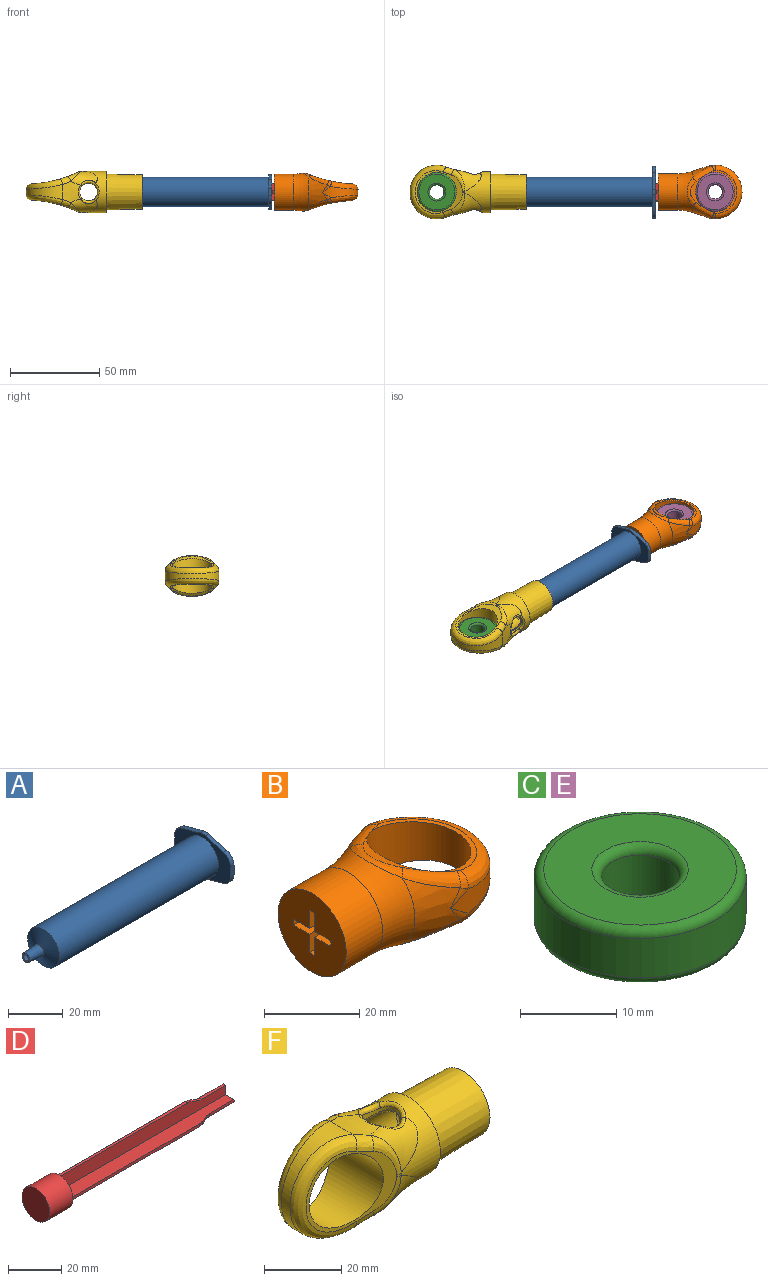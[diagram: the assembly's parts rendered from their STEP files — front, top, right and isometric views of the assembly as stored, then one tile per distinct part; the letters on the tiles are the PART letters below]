
ASSEMBLY  parts=6 mates=10
PART A: 21 faces, bbox 93.5x29x19.6 mm
  f0: cone r=2mm half-angle=3.3deg, axis (1,0,0), area 96.2mm2, adj f1,f6
  f1: plane 4x4mm, normal (-1,0,0), area 7.3mm2, adj f0,f2
  f2: cone r=1.3mm half-angle=3.3deg, axis (1,0,0), area 73.8mm2, adj f1,f3
  f3: cone r=7.31mm half-angle=69deg, axis (1,0,0), area 169.6mm2, adj f2,f4
  f4: cylinder r=7.31mm len=83.65mm, axis (-1,0,0), area 3842.3mm2, adj f3,f13
  f5: cylinder r=8.25mm len=82.5mm, axis (-1,0,0), area 4276.5mm2, adj f6,f14
  f6: cone r=2.4mm half-angle=69deg, axis (1,0,0), area 209.7mm2, adj f0,f5
  f7: plane 4.39x1.8mm, normal (0,-1,0), area 7.9mm2, adj f13,f14,f15,f20
  f8: plane 9.5x2.62mm, normal (0,-0.27,-0.96), area 17.7mm2, adj f13,f14,f15,f16
  f9: plane 9.5x2.62mm, normal (0,0.27,-0.96), area 17.7mm2, adj f13,f14,f16,f17
  f10: plane 4.39x1.8mm, normal (0,1,0), area 7.9mm2, adj f13,f14,f17,f18
  f11: plane 9.5x2.62mm, normal (0,0.27,0.96), area 17.7mm2, adj f13,f14,f18,f19
  f12: plane 9.5x2.62mm, normal (0,-0.27,0.96), area 17.7mm2, adj f13,f14,f19,f20
  f13: plane 29x19.63mm, normal (1,0,0), area 284.7mm2, adj f4,f7,f8,f9,f10,f11,f12,f15
  f14: plane 29x19.63mm, normal (-1,0,0), area 238.8mm2, adj f5,f7,f8,f9,f10,f11,f12,f15
  f15: cylinder r=5mm len=4.82mm, axis (-1,0,0), area 11.7mm2, adj f7,f8,f13,f14
  f16: cylinder r=5mm len=2.66mm, axis (-1,0,0), area 4.8mm2, adj f8,f9,f13,f14
  f17: cylinder r=5mm len=4.82mm, axis (-1,0,0), area 11.7mm2, adj f9,f10,f13,f14
  f18: cylinder r=5mm len=4.82mm, axis (1,0,0), area 11.7mm2, adj f10,f11,f13,f14
  f19: cylinder r=5mm len=2.66mm, axis (-1,0,0), area 4.8mm2, adj f11,f12,f13,f14
  f20: cylinder r=5mm len=4.82mm, axis (1,0,0), area 11.7mm2, adj f7,f12,f13,f14
PART B: 40 faces, bbox 53.9x37.9x37.9 mm
  f0: cylinder r=76.94mm len=17.73mm, axis (0,1,0), area 33.2mm2, adj f23,f37,f38,f39
  f1: cylinder r=76.94mm len=17.73mm, axis (0,1,0), area 33.2mm2, adj f23,f31,f32,f33
  f2: cone r=10.16mm half-angle=18.9deg, axis (1,0,0), area 147.9mm2, adj f5,f25,f27,f32,f38
  f3: cone r=10.16mm half-angle=18.9deg, axis (1,0,0), area 147.9mm2, adj f5,f24,f26,f31,f37
  f4: cylinder r=15mm len=30mm, axis (0,0,-1), area 330mm2, adj f24,f25,f26,f27,f28,f34
  f5: torus R=35.56mm, axis (1,0,0), area 496.2mm2, adj f2,f3,f7,f33,f39
  f6: plane 20.32x20.32mm, normal (-1,0,0), area 293.5mm2, adj f7,f8,f9,f10,f11,f12,f13,f14
  f7: cylinder r=10.16mm len=20.32mm, axis (1,0,0), area 694mm2, adj f5,f6
  f8: plane 12.14x4.75mm, normal (0,0,-1), area 57.7mm2, adj f6,f9,f19,f20
  f9: plane 12.14x4.75mm, normal (0,1,0), area 57.7mm2, adj f6,f8,f10,f20
  f10: plane 12.14x1.5mm, normal (0,0,-1), area 18.2mm2, adj f6,f9,f11,f20
  f11: plane 12.14x4.75mm, normal (0,-1,0), area 57.7mm2, adj f6,f10,f12,f20
  f12: plane 12.14x4.75mm, normal (0,0,-1), area 57.7mm2, adj f6,f11,f13,f20
  f13: plane 12.14x1.5mm, normal (0,-1,0), area 18.2mm2, adj f6,f12,f14,f20
  f14: plane 12.14x4.75mm, normal (0,0,1), area 57.7mm2, adj f6,f13,f15,f20
  f15: plane 12.14x4.75mm, normal (0,-1,0), area 57.7mm2, adj f6,f14,f16,f20
  f16: plane 12.14x1.5mm, normal (0,0,1), area 18.2mm2, adj f6,f15,f17,f20
  f17: plane 12.14x4.75mm, normal (0,1,0), area 57.7mm2, adj f6,f16,f18,f20
  f18: plane 12.14x4.75mm, normal (0,0,1), area 57.7mm2, adj f6,f17,f19,f20
  f19: plane 12.14x1.5mm, normal (0,1,0), area 18.2mm2, adj f6,f8,f18,f20
  f20: plane 11x11mm, normal (-1,0,0), area 30.7mm2, adj f8,f9,f10,f11,f12,f13,f14,f15
  f21: cylinder r=76.94mm len=24mm, axis (0,1,0), area 45.4mm2, adj f23,f34,f35,f36,f37,f38
  f22: cylinder r=76.94mm len=24mm, axis (0,1,0), area 45.3mm2, adj f23,f28,f29,f30,f31,f32
  f23: cylinder r=11mm len=22mm, axis (0,0,-1), area 868.9mm2, adj f0,f1,f21,f22,f31,f32,f37,f38
  f24: bspline ~5.98x5.9mm, area 3.6mm2, adj f3,f4,f35
  f25: bspline ~5.98x5.9mm, area 3.6mm2, adj f2,f4,f30
  f26: bspline ~5.98x5.9mm, area 3.6mm2, adj f3,f4,f29
  f27: bspline ~5.98x5.9mm, area 3.6mm2, adj f2,f4,f36
  f28: bspline ~30.03x17.08mm, area 200.4mm2, adj f4,f22,f29,f30
  f29: bspline ~3.54x3.48mm, area 7.3mm2, adj f22,f26,f28,f31
  f30: bspline ~4.63x4.11mm, area 7.3mm2, adj f22,f25,f28,f32
  f31: bspline ~12.09x8.67mm, area 46.5mm2, adj f1,f3,f22,f23,f29,f33
  f32: bspline ~12.09x8.67mm, area 46.5mm2, adj f1,f2,f22,f23,f30,f33
  f33: bspline ~18.8x6.62mm, area 36.3mm2, adj f1,f5,f31,f32
  f34: bspline ~30.03x17.08mm, area 200.4mm2, adj f4,f21,f35,f36
  f35: bspline ~3.62x3.55mm, area 7.3mm2, adj f21,f24,f34,f37
  f36: bspline ~4.63x4.11mm, area 7.3mm2, adj f21,f27,f34,f38
  f37: bspline ~12.09x8.67mm, area 46.5mm2, adj f0,f3,f21,f23,f35,f39
  f38: bspline ~12.09x8.67mm, area 46.5mm2, adj f0,f2,f21,f23,f36,f39
  f39: bspline ~18.8x6.62mm, area 36.3mm2, adj f0,f5,f37,f38
PART C: 8 faces, bbox 23.8x23.8x7 mm
  f0: cylinder r=4mm len=8mm, axis (0,0,-1), area 125.7mm2, adj f4,f6
  f1: cylinder r=11mm len=22mm, axis (0,0,-1), area 345.6mm2, adj f5,f7
  f2: plane 20x20mm, normal (0,0,1), area 235.6mm2, adj f6,f7
  f3: plane 20x20mm, normal (0,0,-1), area 235.6mm2, adj f4,f5
  f4: torus R=5mm, axis (0,0,1), area 43.1mm2, adj f0,f3
  f5: torus R=10mm, axis (0,0,1), area 105mm2, adj f1,f3
  f6: torus R=5mm, axis (0,0,1), area 43.1mm2, adj f0,f2
  f7: torus R=10mm, axis (0,0,1), area 105mm2, adj f1,f2
PART D: 32 faces, bbox 100.6x15.2x15.2 mm
  f0: plane 10x10mm, normal (1,0,0), area 23.7mm2, adj f1,f2,f3,f4,f5,f6,f7,f8
  f1: plane 88.18x6.94mm, normal (0,-1,0), area 523.6mm2, adj f0,f5,f12,f15,f16,f17,f29,f30
  f2: plane 88.18x6.95mm, normal (0,1,0), area 523.6mm2, adj f0,f3,f12,f15,f16,f17,f29,f30
  f3: plane 88.18x6.94mm, normal (0,0,1), area 523.6mm2, adj f0,f2,f11,f15,f18,f19,f26,f31
  f4: plane 88.18x6.95mm, normal (0,0,-1), area 523.6mm2, adj f0,f6,f11,f15,f18,f19,f26,f31
  f5: plane 88.18x6.95mm, normal (0,0,1), area 523.6mm2, adj f0,f1,f9,f15,f22,f23,f24,f28
  f6: plane 88.18x6.94mm, normal (0,1,0), area 523.6mm2, adj f0,f4,f10,f15,f20,f21,f25,f27
  f7: plane 88.18x6.95mm, normal (0,-1,0), area 523.6mm2, adj f0,f8,f10,f15,f20,f21,f25,f27
  f8: plane 88.18x6.94mm, normal (0,0,-1), area 523.6mm2, adj f0,f7,f9,f15,f22,f23,f24,f28
  f9: plane 67.42x1.27mm, normal (0,-1,0), area 85.5mm2, adj f5,f8,f15,f24
  f10: plane 67.42x1.27mm, normal (0,0,-1), area 85.5mm2, adj f6,f7,f15,f25
  f11: plane 67.42x1.27mm, normal (0,1,0), area 85.5mm2, adj f3,f4,f15,f26
  f12: plane 67.42x1.27mm, normal (0,0,1), area 85.5mm2, adj f1,f2,f15,f30
  f13: cylinder r=7.3mm len=14.6mm, axis (-1,0,0), area 568.8mm2, adj f14,f15
  f14: plane 14.6x14.6mm, normal (-1,0,0), area 167.4mm2, adj f13
  f15: plane 14.6x14.6mm, normal (1,0,0), area 133.5mm2, adj f1,f2,f3,f4,f5,f6,f7,f8
  f16: cone r=5mm half-angle=20.8deg, axis (-1,0,0), area 4.9mm2, adj f1,f2,f29,f30
  f17: cylinder r=5mm len=13.08mm, axis (1,0,0), area 16.7mm2, adj f0,f1,f2,f29
  f18: cone r=5mm half-angle=20.8deg, axis (-1,0,0), area 4.9mm2, adj f3,f4,f26,f31
  f19: cylinder r=5mm len=13.08mm, axis (1,0,0), area 16.7mm2, adj f0,f3,f4,f31
  f20: cone r=5mm half-angle=20.8deg, axis (-1,0,0), area 4.9mm2, adj f6,f7,f25,f27
  f21: cylinder r=5mm len=13.08mm, axis (1,0,0), area 16.7mm2, adj f0,f6,f7,f27
  f22: cylinder r=5mm len=13.08mm, axis (1,0,0), area 16.7mm2, adj f0,f5,f8,f28
  f23: cone r=5mm half-angle=20.8deg, axis (-1,0,0), area 4.9mm2, adj f5,f8,f24,f28
  f24: bspline ~5.19x2.26mm, area 3.2mm2, adj f5,f8,f9,f23
  f25: bspline ~5.19x2.26mm, area 3.2mm2, adj f6,f7,f10,f20
  f26: bspline ~5.19x2.26mm, area 3.2mm2, adj f3,f4,f11,f18
  f27: torus R=10mm, axis (1,0,0), area 2.3mm2, adj f6,f7,f20,f21
  f28: torus R=10mm, axis (1,0,0), area 2.3mm2, adj f5,f8,f22,f23
  f29: torus R=10mm, axis (1,0,0), area 2.3mm2, adj f1,f2,f16,f17
  f30: bspline ~5.19x2.26mm, area 3.2mm2, adj f1,f2,f12,f16
  f31: torus R=10mm, axis (1,0,0), area 2.3mm2, adj f3,f4,f18,f19
PART E: same geometry as C
PART F: 48 faces, bbox 65x23x31.8 mm
  f0: cylinder r=11.5mm len=23mm, axis (-1,0,0), area 496.9mm2, adj f9,f11,f12,f14,f19,f26,f37,f44
  f1: cylinder r=8.5mm len=17mm, axis (-1,0,0), area 644.9mm2, adj f4,f31
  f2: cylinder r=15mm len=30mm, axis (0,1,0), area 489.5mm2, adj f10,f13,f36,f41
  f3: cylinder r=8.5mm len=21.57mm, axis (-1,0,0), area 865mm2, adj f5,f21,f22,f30
  f4: plane 19.3x19.3mm, normal (1,0,0), area 65.6mm2, adj f1,f46
  f5: cylinder r=15mm len=17mm, axis (0,1,0), area 237.5mm2, adj f3
  f6: cylinder r=67.79mm len=26.51mm, axis (0,0,1), area 123.1mm2, adj f8,f40,f41,f42,f43,f44,f45
  f7: cylinder r=67.79mm len=26.51mm, axis (0,0,1), area 123.2mm2, adj f8,f34,f35,f36,f37,f38,f39
  f8: cylinder r=11mm len=22mm, axis (0,1,0), area 854.3mm2, adj f6,f7
  f9: bspline ~19.73x14.07mm, area 125.1mm2, adj f0,f10,f20,f42
  f10: bspline ~21.21x16.36mm, area 97.7mm2, adj f2,f9,f11,f18,f34,f40
  f11: bspline ~20.03x14.18mm, area -5.5mm2, adj f0,f10,f17,f35
  f12: bspline ~19.73x14.07mm, area 125.1mm2, adj f0,f13,f25,f39
  f13: bspline ~21.21x16.36mm, area 97.7mm2, adj f2,f12,f14,f23,f38,f43
  f14: bspline ~20.03x14.18mm, area -5.5mm2, adj f0,f13,f24,f45
  f15: cylinder r=5mm len=10mm, axis (0,0,1), area 41.6mm2, adj f21,f23,f24,f25,f26
  f16: cylinder r=5mm len=10mm, axis (0,0,1), area 41.6mm2, adj f17,f18,f19,f20,f22
  f17: bspline ~9.81x4.36mm, area 17.4mm2, adj f11,f16,f18,f19
  f18: bspline ~9.56x2.84mm, area 10.6mm2, adj f10,f16,f17,f20
  f19: bspline ~11.45x3.9mm, area 16.4mm2, adj f0,f16,f17,f20
  f20: bspline ~9.81x4.36mm, area 17.4mm2, adj f9,f16,f18,f19
  f21: bspline ~12.01x10.74mm, area 41.9mm2, adj f3,f15
  f22: bspline ~12.01x10.74mm, area 41.9mm2, adj f3,f16
  f23: bspline ~9.56x2.84mm, area 10.6mm2, adj f13,f15,f24,f25
  f24: bspline ~9.81x4.36mm, area 17.4mm2, adj f14,f15,f23,f26
  f25: bspline ~9.81x4.36mm, area 17.4mm2, adj f12,f15,f23,f26
  f26: bspline ~11.45x3.9mm, area 16.4mm2, adj f0,f15,f24,f25
  f27: plane 16x16mm, normal (1,0,0), area 81.4mm2, adj f31,f32
  f28: plane 16x16mm, normal (-1,0,0), area 81.4mm2, adj f30,f33
  f29: cylinder r=5.67mm len=11.34mm, axis (-1,0,0), area 71.3mm2, adj f32,f33
  f30: torus R=8mm, axis (-1,0,0), area 41mm2, adj f3,f28
  f31: torus R=8mm, axis (-1,0,0), area 41mm2, adj f1,f27
  f32: torus R=6.17mm, axis (-1,0,0), area 28.9mm2, adj f27,f29
  f33: torus R=6.17mm, axis (-1,0,0), area 28.9mm2, adj f28,f29
  f34: bspline ~14.87x7.81mm, area 25.1mm2, adj f7,f10,f35,f36
  f35: bspline ~12.84x8.13mm, area 36mm2, adj f7,f11,f34,f37
  f36: bspline ~30.03x22.1mm, area 247.9mm2, adj f2,f7,f34,f38
  f37: bspline ~3.12x1.45mm, area 0.8mm2, adj f0,f7,f35,f39
  f38: bspline ~14.83x7.79mm, area 25.1mm2, adj f7,f13,f36,f39
  f39: bspline ~12.94x8.25mm, area 36mm2, adj f7,f12,f37,f38
  f40: bspline ~14.83x7.79mm, area 25.1mm2, adj f6,f10,f41,f42
  f41: bspline ~30.03x22.1mm, area 247.9mm2, adj f2,f6,f40,f43
  f42: bspline ~12.94x8.25mm, area 36mm2, adj f6,f9,f40,f44
  f43: bspline ~14.87x7.81mm, area 25.1mm2, adj f6,f13,f41,f45
  f44: bspline ~3.12x1.45mm, area 0.8mm2, adj f0,f6,f42,f45
  f45: bspline ~12.84x8.13mm, area 36mm2, adj f6,f14,f43,f44
  f46: cone r=10mm half-angle=1deg, axis (-1,0,0), area 1234.9mm2, adj f4,f47
  f47: plane 23x23mm, normal (1,0,0), area 101.3mm2, adj f0,f46
PLACE A rot(axis=(-0.31,0.13,0.94),0deg) t=(0.1,0.02,-0.03)mm fixed
PLACE B rot(axis=(-0.31,0.13,0.94),0deg) t=(126.83,0.14,-0.15)mm
PLACE C t=(-29,0.02,-3.65)mm
PLACE D rot(axis=(-1,0,0),90deg) t=(7.22,0.02,-0.03)mm
PLACE E t=(126.83,0.14,-3.65)mm
PLACE F rot(axis=(1,0,0),90deg) t=(-29,0.02,-0.03)mm
MATE pin_slot B.f23 <-> E.f1  axis (0,0,-1) through (126.83,0.14,-0.15)mm
MATE slider D.f13 <-> A.f0  axis (-1,0,0) through (7.22,0.02,-0.03)mm
MATE planar C.f1 <-> E.f1  axis (0,0,-1) through (-29,0.02,-3.65)mm
MATE planar A.f0 <-> F.f0  axis (-1,0,0) through (0.1,0.02,-0.03)mm
MATE planar D.f8 <-> B.f9  axis (0,-1,0) through (61.12,-0.61,3.64)mm
MATE planar D.f7 <-> B.f8  axis (0,0,1) through (61.12,-3.65,0.6)mm
MATE slider B.f23 <-> E.f1  axis (0,0,-1) through (126.83,0.14,-0.15)mm
MATE planar B.f5 <-> D.f16  axis (-1,0,0) through (107.22,0.14,-0.15)mm
MATE cylindrical C.f1 <-> F.f8  axis (0,0,-1) through (-29,0.02,-0.15)mm
MATE cylindrical A.f0 <-> F.f0  axis (-1,0,0) through (50.55,0.02,-0.03)mm
